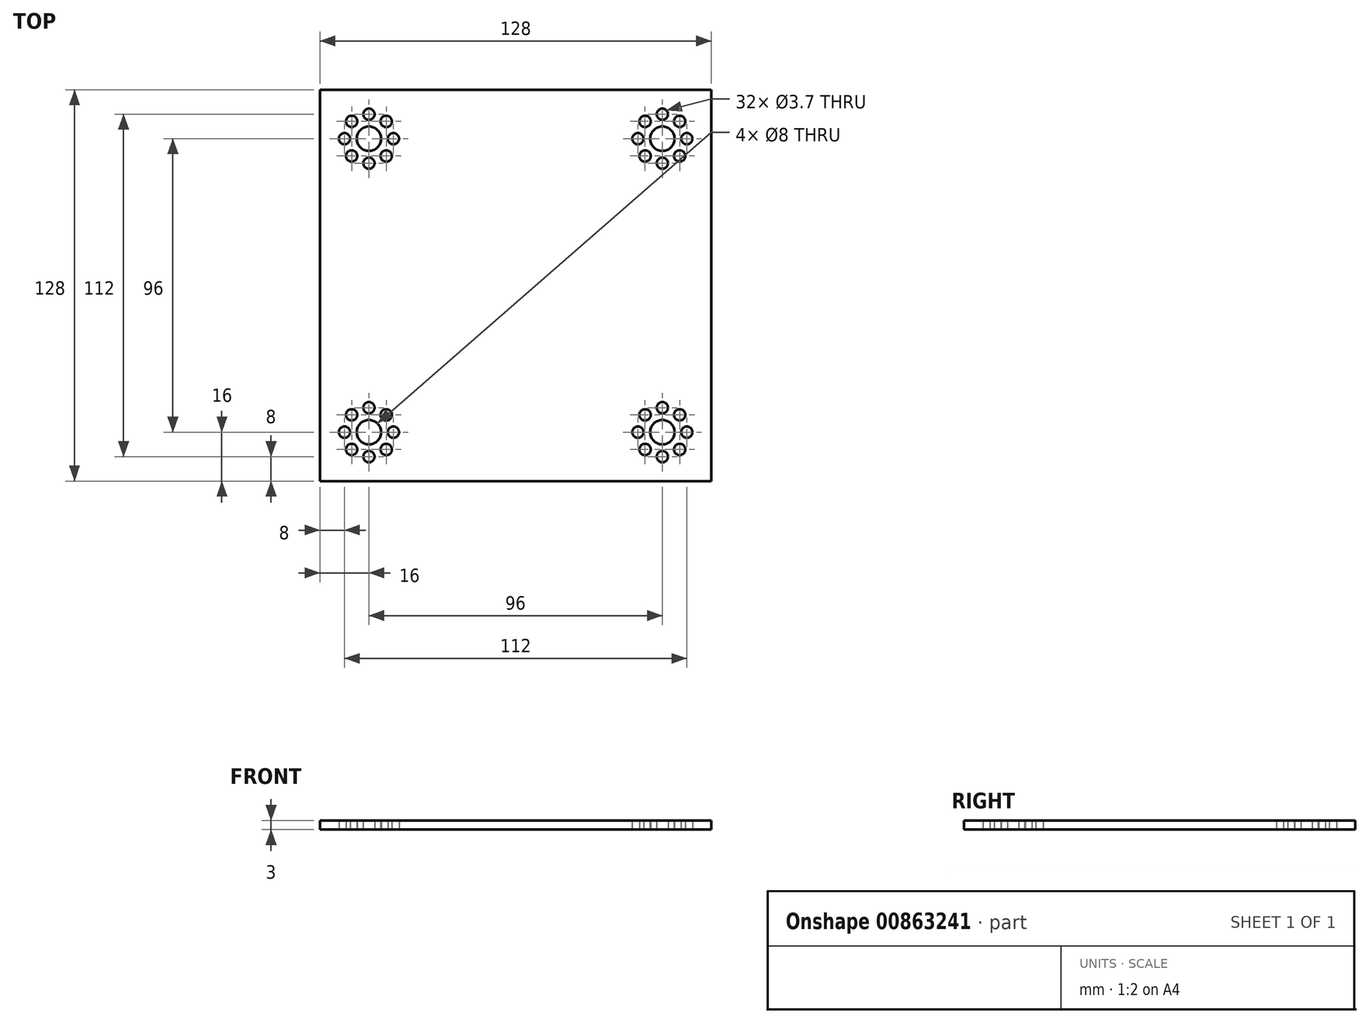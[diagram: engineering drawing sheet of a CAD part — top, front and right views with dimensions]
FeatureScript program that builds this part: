
annotation { "Feature Type Name" : "Feature", "Feature Type Description" : "" }
export const myFeature = defineFeature(function(context is Context, id is Id, definition is map)
    precondition{}
    {
        {
            var Q0;
            Q0=qCreatedBy(makeId("Top.planeOp"),FACE);
            var sketch = newSketch(context, id + "F0", { "sketchPlane" : qUnion([Q0])});
            skLineSegment(sketch, "E0.bottom", {"start": v(-64, 64) * mm, "end": v(64, 64) * mm});
            skLineSegment(sketch, "E0.top", {"start": v(-64, -64) * mm, "end": v(64, -64) * mm});
            skLineSegment(sketch, "E0.left", {"start": v(-64, 64) * mm, "end": v(-64, -64) * mm});
            skLineSegment(sketch, "E0.right", {"start": v(64, 64) * mm, "end": v(64, -64) * mm});
            skPoint(sketch, "E0.middle", {"position": v(0, 0) * mm});
            skCircle(sketch, "E1", {"center": v(-48, 48) * mm, "radius": 4 * mm});
            skCircle(sketch, "E2", {"center": v(-40, 48) * mm, "radius": 1.85 * mm});
            skCircle(sketch, "E3.1.0", {"center": v(-42.34, 53.66) * mm, "radius": 1.85 * mm});
            skCircle(sketch, "E3.2.0", {"center": v(-48, 56) * mm, "radius": 1.85 * mm});
            skCircle(sketch, "E3.3.0", {"center": v(-53.66, 53.66) * mm, "radius": 1.85 * mm});
            skCircle(sketch, "E3.4.0", {"center": v(-56, 48) * mm, "radius": 1.85 * mm});
            skCircle(sketch, "E3.5.0", {"center": v(-53.66, 42.34) * mm, "radius": 1.85 * mm});
            skCircle(sketch, "E3.6.0", {"center": v(-48, 40) * mm, "radius": 1.85 * mm});
            skCircle(sketch, "E3.7.0", {"center": v(-42.34, 42.34) * mm, "radius": 1.85 * mm});
            skPoint(sketch, "E4.MirrorP", {"position": v(48, 48) * mm});
            skCircle(sketch, "E5.MirrorC", {"center": v(40, 48) * mm, "radius": 1.85 * mm});
            skCircle(sketch, "E6.MirrorC", {"center": v(42.34, 42.34) * mm, "radius": 1.85 * mm});
            skCircle(sketch, "E7.MirrorC", {"center": v(48, 56) * mm, "radius": 1.85 * mm});
            skCircle(sketch, "E8.MirrorC", {"center": v(53.66, 53.66) * mm, "radius": 1.85 * mm});
            skCircle(sketch, "E9.MirrorC", {"center": v(48, 48) * mm, "radius": 4 * mm});
            skCircle(sketch, "E10.MirrorC", {"center": v(56, 48) * mm, "radius": 1.85 * mm});
            skCircle(sketch, "E11.MirrorC", {"center": v(48, 40) * mm, "radius": 1.85 * mm});
            skCircle(sketch, "E12.MirrorC", {"center": v(53.66, 42.34) * mm, "radius": 1.85 * mm});
            skCircle(sketch, "E13.MirrorC", {"center": v(42.34, 53.66) * mm, "radius": 1.85 * mm});
            skCircle(sketch, "E14.MirrorC", {"center": v(-42.34, -42.34) * mm, "radius": 1.85 * mm});
            skCircle(sketch, "E15.MirrorC", {"center": v(-48, -40) * mm, "radius": 1.85 * mm});
            skCircle(sketch, "E16.MirrorC", {"center": v(42.34, -42.34) * mm, "radius": 1.85 * mm});
            skCircle(sketch, "E17.MirrorC", {"center": v(53.66, -53.66) * mm, "radius": 1.85 * mm});
            skPoint(sketch, "E18.MirrorP", {"position": v(-48, -48) * mm});
            skCircle(sketch, "E19.MirrorC", {"center": v(-53.66, -42.34) * mm, "radius": 1.85 * mm});
            skCircle(sketch, "E20.MirrorC", {"center": v(40, -48) * mm, "radius": 1.85 * mm});
            skCircle(sketch, "E21.MirrorC", {"center": v(48, -48) * mm, "radius": 4 * mm});
            skCircle(sketch, "E22.MirrorC", {"center": v(-56, -48) * mm, "radius": 1.85 * mm});
            skCircle(sketch, "E23.MirrorC", {"center": v(48, -56) * mm, "radius": 1.85 * mm});
            skCircle(sketch, "E24.MirrorC", {"center": v(56, -48) * mm, "radius": 1.85 * mm});
            skCircle(sketch, "E25.MirrorC", {"center": v(-53.66, -53.66) * mm, "radius": 1.85 * mm});
            skCircle(sketch, "E26.MirrorC", {"center": v(48, -40) * mm, "radius": 1.85 * mm});
            skCircle(sketch, "E27.MirrorC", {"center": v(-48, -56) * mm, "radius": 1.85 * mm});
            skCircle(sketch, "E28.MirrorC", {"center": v(53.66, -42.34) * mm, "radius": 1.85 * mm});
            skCircle(sketch, "E29.MirrorC", {"center": v(-42.34, -53.66) * mm, "radius": 1.85 * mm});
            skCircle(sketch, "E30.MirrorC", {"center": v(42.34, -53.66) * mm, "radius": 1.85 * mm});
            skCircle(sketch, "E31.MirrorC", {"center": v(-48, -48) * mm, "radius": 4 * mm});
            skCircle(sketch, "E32.MirrorC", {"center": v(-40, -48) * mm, "radius": 1.85 * mm});
            skSolve(sketch);
        }
        {
            var Q0;
            Q0 = qSketchRegion(id + "F0", true);
            extrude(context, id + "F1", {"entities" : qUnion([Q0]), "depth" : 3 * mm, "offsetDistance" : 25 * mm});
        }
    });
